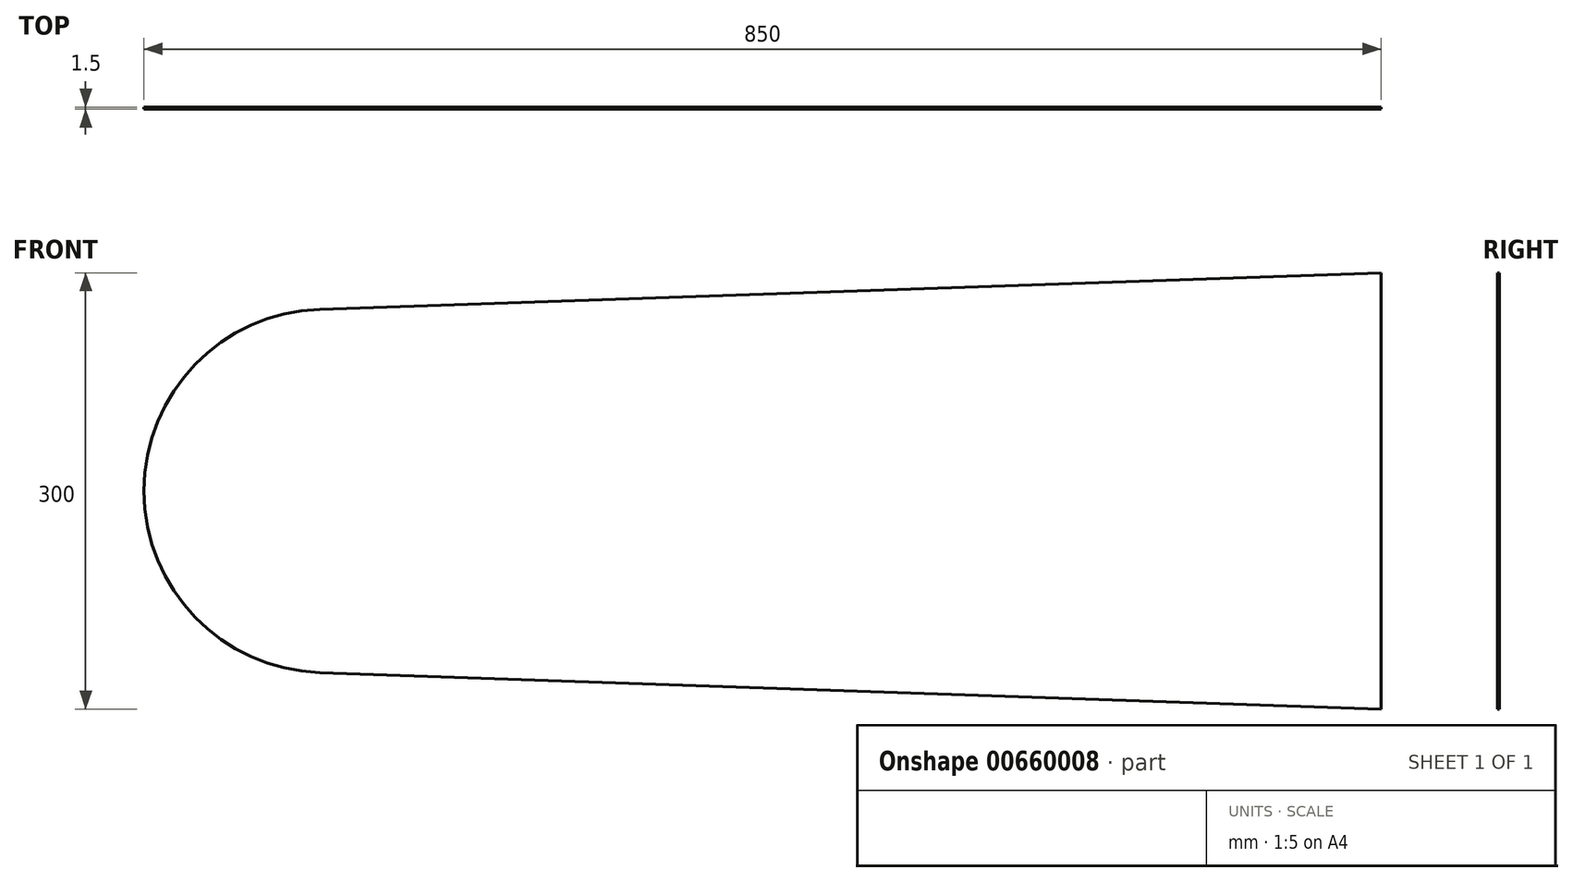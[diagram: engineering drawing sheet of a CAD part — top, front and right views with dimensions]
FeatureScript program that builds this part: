
annotation { "Feature Type Name" : "Feature", "Feature Type Description" : "" }
export const myFeature = defineFeature(function(context is Context, id is Id, definition is map)
    precondition{}
    {
        {
            var Q0;
            Q0=qCreatedBy(makeId("Front.planeOp"),FACE);
            var sketch = newSketch(context, id + "F0", { "sketchPlane" : qUnion([Q0])});
            skCircle(sketch, "E0", {"center": v(-725, 0) * mm, "radius": 125 * mm});
            skLineSegment(sketch, "E1", {"start": v(0, 0) * mm, "end": v(-725, 0) * mm});
            skLineSegment(sketch, "E2", {"start": v(0, 150) * mm, "end": v(-729.3, 124.93) * mm});
            skLineSegment(sketch, "E3", {"start": v(0, -150) * mm, "end": v(-729.3, -124.93) * mm});
            skLineSegment(sketch, "E4", {"start": v(0, 0) * mm, "end": v(0, 150) * mm});
            skLineSegment(sketch, "E5", {"start": v(0, 0) * mm, "end": v(0, -150) * mm});
            skSolve(sketch);
        }
        {
            var Q0;
            {var subQ0=sQuery(id+"F0.wireOp",EDGE,"E1");var subQ1=sQuery(id+"F0.wireOp",EDGE,"ZFQ2gco3-H9qs-s49o-krYr-cHRq3sGXDUtx");var subQ2=makeQuery(id+"F0.imprint","INTERSECT",VERTEX,{"derivedFrom":[subQ1,subQ0]});Q0=makeQuery(id+"F0.imprint","IMPRINT",FACE,{"disambiguationData":[TD([[makeQuery(id+"F0.imprint","IMPRINT",EDGE,{"disambiguationData":[TD([[subQ2,-1.0]])],"derivedFrom":subQ1}),-1.0]])]});}
            var Q1;
            {var subQ0=sQuery(id+"F0.wireOp",EDGE,"E2");var subQ1=sQuery(id+"F0.wireOp",EDGE,"ZFQ2gco3-H9qs-s49o-krYr-cHRq3sGXDUtx");var subQ7=makeQuery(id+"F0.imprint","INTERSECT",VERTEX,{"disambiguationData":[OD(1.0)],"derivedFrom":[subQ1,subQ0]});Q1=makeQuery(id+"F0.imprint","IMPRINT",FACE,{"disambiguationData":[TD([[makeQuery(id+"F0.imprint","IMPRINT",EDGE,{"disambiguationData":[TD([[subQ7,-1.0]])],"derivedFrom":subQ1}),1.0]])]});}
            var Q2;
            {var subQ0=sQuery(id+"F0.wireOp",EDGE,"E2");var subQ1=sQuery(id+"F0.wireOp",EDGE,"ZFQ2gco3-H9qs-s49o-krYr-cHRq3sGXDUtx");var subQ2=makeQuery(id+"F0.imprint","INTERSECT",VERTEX,{"disambiguationData":[OD(1.0)],"derivedFrom":[subQ1,subQ0]});Q2=makeQuery(id+"F0.imprint","IMPRINT",FACE,{"disambiguationData":[TD([[makeQuery(id+"F0.imprint","IMPRINT",EDGE,{"disambiguationData":[TD([[subQ2,-1.0]])],"derivedFrom":subQ1}),-1.0]])]});}
            var Q3;
            {var subQ0=sQuery(id+"F0.wireOp",EDGE,"E0");var subQ1=makeQuery(id+"F0.imprint","INTERSECT",VERTEX,{"derivedFrom":[subQ0,sQuery(id+"F0.wireOp",EDGE,"E3")]});Q3=makeQuery(id+"F0.imprint","IMPRINT",FACE,{"disambiguationData":[TD([[makeQuery(id+"F0.imprint","IMPRINT",EDGE,{"disambiguationData":[TD([[subQ1,1.0]])],"derivedFrom":subQ0}),1.0]])]});}
            var Q4;
            {var subQ0=sQuery(id+"F0.wireOp",EDGE,"E0");var subQ1=makeQuery(id+"F0.imprint","INTERSECT",VERTEX,{"derivedFrom":[subQ0,sQuery(id+"F0.wireOp",EDGE,"E2")]});Q4=makeQuery(id+"F0.imprint","IMPRINT",FACE,{"disambiguationData":[TD([[makeQuery(id+"F0.imprint","IMPRINT",EDGE,{"disambiguationData":[TD([[subQ1,1.0]])],"derivedFrom":subQ0}),1.0]])]});}
            var Q5;
            {var subQ0=sQuery(id+"F0.wireOp",EDGE,"E3");Q5=makeQuery(id+"F0.imprint","IMPRINT",FACE,{"disambiguationData":[TD([[makeQuery(id+"F0.imprint","IMPRINT",EDGE,{"derivedFrom":subQ0}),-1.0]])]});}
            var Q6;
            {var subQ0=sQuery(id+"F0.wireOp",EDGE,"E2");Q6=makeQuery(id+"F0.imprint","IMPRINT",FACE,{"disambiguationData":[TD([[makeQuery(id+"F0.imprint","IMPRINT",EDGE,{"derivedFrom":subQ0}),1.0]])]});}
            extrude(context, id + "F1", {"entities" : qUnion([Q0, Q1, Q2, Q3, Q4, Q5, Q6]), "endBound" : BoundingType.SYMMETRIC, "depth" : 1.5 * mm, "offsetDistance" : 25 * mm});
        }
    });
